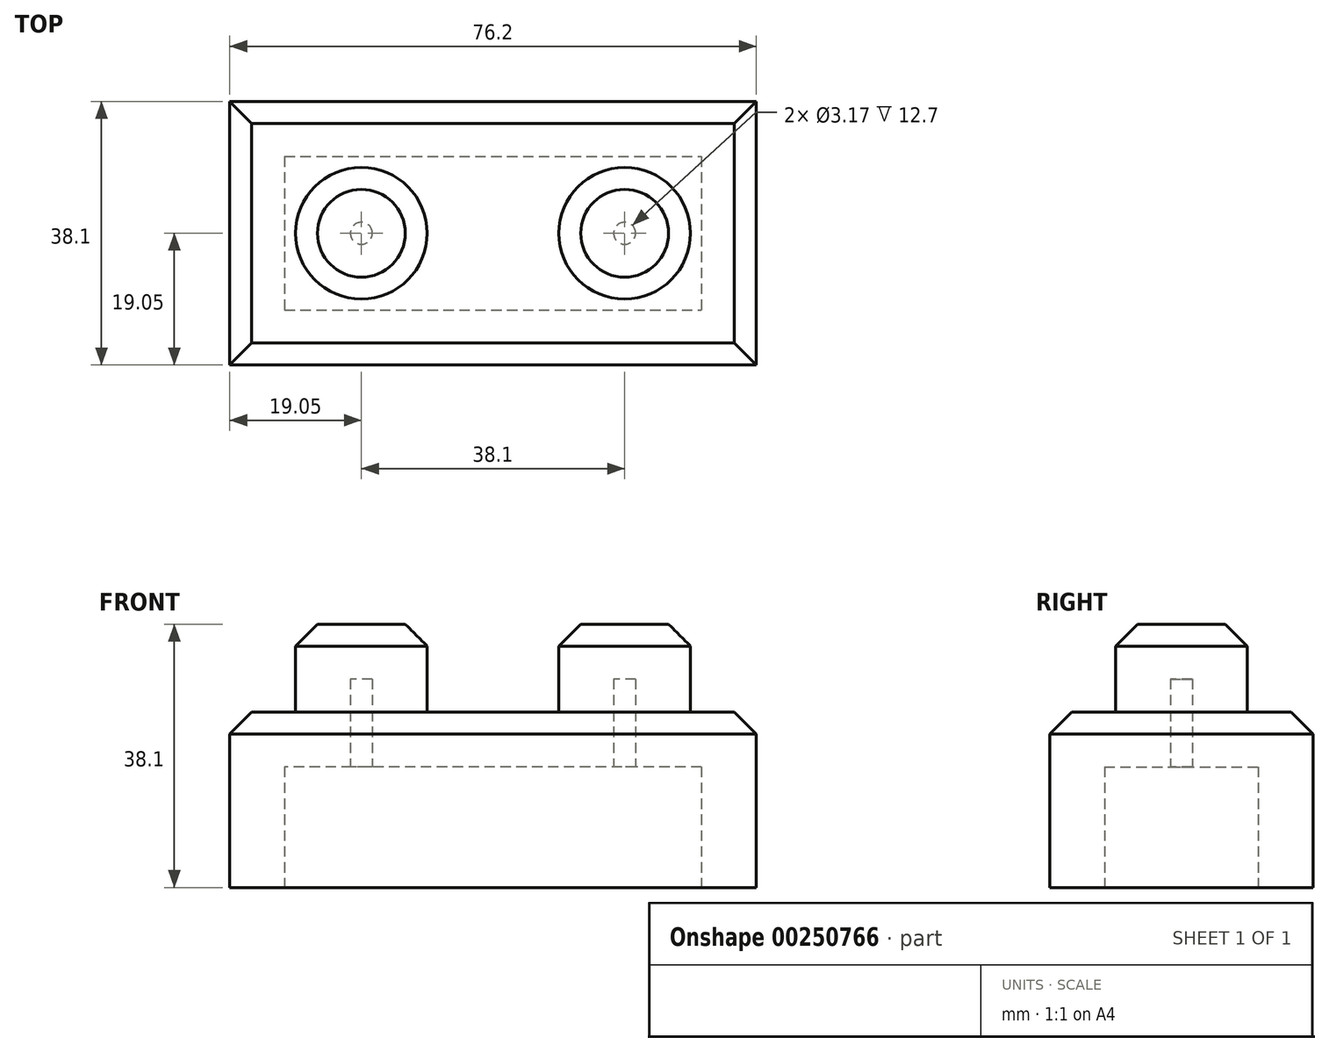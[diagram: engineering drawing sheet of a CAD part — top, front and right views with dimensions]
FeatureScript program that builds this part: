
annotation { "Feature Type Name" : "Feature", "Feature Type Description" : "" }
export const myFeature = defineFeature(function(context is Context, id is Id, definition is map)
    precondition{}
    {
        {
            var Q0;
            Q0=qCreatedBy(makeId("Top.planeOp"),FACE);
            var sketch = newSketch(context, id + "F0", { "sketchPlane" : qUnion([Q0])});
            skLineSegment(sketch, "E0.bottom", {"start": v(0, 0) * mm, "end": v(76.2, 0) * mm});
            skLineSegment(sketch, "E0.top", {"start": v(0, -38.1) * mm, "end": v(76.2, -38.1) * mm});
            skLineSegment(sketch, "E0.left", {"start": v(0, 0) * mm, "end": v(0, -38.1) * mm});
            skLineSegment(sketch, "E0.right", {"start": v(76.2, 0) * mm, "end": v(76.2, -38.1) * mm});
            skSolve(sketch);
        }
        {
            var Q0;
            Q0=makeQuery(id+"F0.imprint","IMPRINT",FACE,{"disambiguationData":[TD([[makeQuery(id+"F0.imprint","IMPRINT",EDGE,{"derivedFrom":sQuery(id+"F0.wireOp",EDGE,"E0.bottom")}),-1.0]])]});
            extrude(context, id + "F1", {"entities" : qUnion([Q0]), "depth" : 25.4 * mm});
        }
        {
            var Q0;
            Q0=makeQuery(id+"F1.opExtrude","CAP_FACE",FACE,{"disambiguationData":[OSD([sQuery(id+"F0.wireOp",EDGE,"E0.bottom"),sQuery(id+"F0.wireOp",EDGE,"E0.top"),sQuery(id+"F0.wireOp",EDGE,"E0.left"),sQuery(id+"F0.wireOp",EDGE,"E0.right")])],"isStart":false});
            var sketch = newSketch(context, id + "F2", { "sketchPlane" : qUnion([Q0])});
            skCircle(sketch, "E1", {"center": v(19.05, -19.05) * mm, "radius": 9.53 * mm});
            skCircle(sketch, "E2", {"center": v(57.15, -19.05) * mm, "radius": 9.53 * mm});
            skSolve(sketch);
        }
        {
            var Q0;
            Q0=makeQuery(id+"F2.imprint","IMPRINT",FACE,{"disambiguationData":[TD([[makeQuery(id+"F2.imprint","IMPRINT",EDGE,{"derivedFrom":sQuery(id+"F2.wireOp",EDGE,"E1")}),1.0]])]});
            var Q1;
            Q1=makeQuery(id+"F2.imprint","IMPRINT",FACE,{"disambiguationData":[TD([[makeQuery(id+"F2.imprint","IMPRINT",EDGE,{"derivedFrom":sQuery(id+"F2.wireOp",EDGE,"E2")}),1.0]])]});
            extrude(context, id + "F3", {"entities" : qUnion([Q0, Q1]), "operationType" : NewBodyOperationType.ADD, "depth" : 12.7 * mm});
        }
        {
            var Q0;
            Q0=makeQuery(id+"F3.opExtrude","CAP_EDGE",EDGE,{"disambiguationData":[OSD([sQuery(id+"F2.wireOp",EDGE,"E2")])],"isStart":false});
            var Q1;
            Q1=makeQuery(id+"F3.opExtrude","CAP_EDGE",EDGE,{"disambiguationData":[OSD([sQuery(id+"F2.wireOp",EDGE,"E1")])],"isStart":false});
            var Q2;
            Q2=makeQuery(id+"F1.opExtrude","CAP_EDGE",EDGE,{"disambiguationData":[OSD([sQuery(id+"F0.wireOp",EDGE,"E0.top")])],"isStart":false});
            var Q3;
            Q3=makeQuery(id+"F1.opExtrude","CAP_EDGE",EDGE,{"disambiguationData":[OSD([sQuery(id+"F0.wireOp",EDGE,"E0.right")])],"isStart":false});
            var Q4;
            Q4=makeQuery(id+"F1.opExtrude","CAP_EDGE",EDGE,{"disambiguationData":[OSD([sQuery(id+"F0.wireOp",EDGE,"E0.bottom")])],"isStart":false});
            var Q5;
            Q5=makeQuery(id+"F1.opExtrude","CAP_EDGE",EDGE,{"disambiguationData":[OSD([sQuery(id+"F0.wireOp",EDGE,"E0.left")])],"isStart":false});
            chamfer(context, id + "F4", {"entities" : qUnion([Q0, Q1, Q2, Q3, Q4, Q5]), "chamferType" : ChamferType.OFFSET_ANGLE, "width" : 3.17 * mm, "oppositeDirection" : false, "angle" : 45 * degree, "tangentPropagation" : true});
        }
        {
            var Q0;
            Q0=makeQuery(id+"F1.opExtrude","CAP_FACE",FACE,{"disambiguationData":[OSD([sQuery(id+"F0.wireOp",EDGE,"E0.bottom"),sQuery(id+"F0.wireOp",EDGE,"E0.top"),sQuery(id+"F0.wireOp",EDGE,"E0.left"),sQuery(id+"F0.wireOp",EDGE,"E0.right")])],"isStart":true});
            shell(context, id + "F5", {"entities" : qUnion([Q0]), "thickness" : 7.94 * mm});
        }
    });
